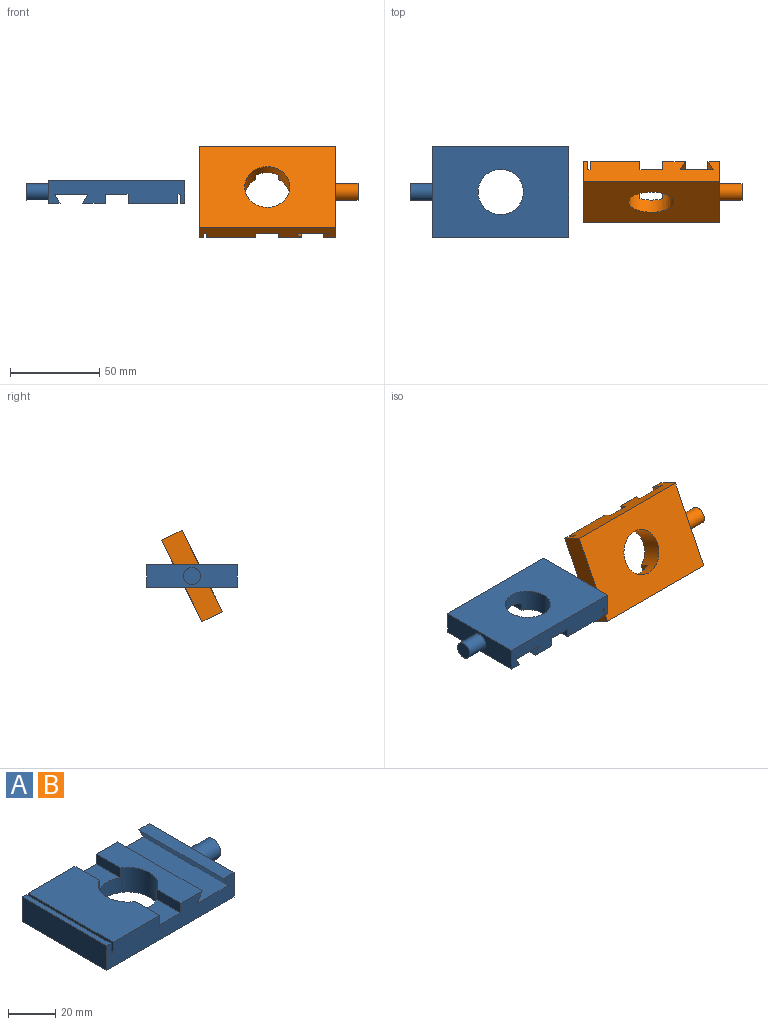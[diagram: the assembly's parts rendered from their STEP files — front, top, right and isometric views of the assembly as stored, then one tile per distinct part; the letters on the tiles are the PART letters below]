
ASSEMBLY  parts=2 mates=1
PART A: 24 faces, bbox 88.9x50.8x12.7 mm
  f0: plane 50.8x6.35mm, normal (0,0,1), area 322.6mm2, adj f1,f2,f7,f21
  f1: plane 76.2x12.7mm, normal (0,-1,0), area 817.4mm2, adj f0,f4,f5,f6,f7,f8,f9,f10
  f2: plane 76.2x12.7mm, normal (0,1,0), area 817.4mm2, adj f0,f4,f5,f6,f7,f8,f9,f13
  f3: cylinder r=12.7mm len=25.4mm, axis (0,0,-1), area 878.3mm2, adj f4,f8,f9,f10,f11,f12,f13,f14
  f4: plane 50.8x27.94mm, normal (0,0,1), area 1320.3mm2, adj f1,f2,f3,f10,f13,f17
  f5: plane 50.8x2.54mm, normal (0,0,1), area 129mm2, adj f1,f2,f6,f16
  f6: plane 50.8x12.7mm, normal (-1,0,0), area 645.2mm2, adj f1,f2,f5,f9
  f7: plane 50.8x12.7mm, normal (1,0,0), area 573.9mm2, adj f0,f1,f2,f9,f22
  f8: plane 50.8x12.7mm, normal (0,0,1), area 546.1mm2, adj f1,f2,f3,f11,f14,f19
  f9: plane 76.2x50.8mm, normal (0,0,-1), area 3364.3mm2, adj f1,f2,f3,f6,f7
  f10: plane 14.4x5.08mm, normal (1,0,0), area 73.2mm2, adj f1,f3,f4,f12
  f11: plane 14.4x5.08mm, normal (-1,0,0), area 73.2mm2, adj f1,f3,f8,f12
  f12: plane 14.4x12.7mm, normal (0,0,1), area 168.3mm2, adj f1,f3,f10,f11
  f13: plane 14.4x5.08mm, normal (1,0,0), area 73.2mm2, adj f2,f3,f4,f15
  f14: plane 14.4x5.08mm, normal (-1,0,0), area 73.2mm2, adj f2,f3,f8,f15
  f15: plane 14.4x12.7mm, normal (0,0,1), area 168.3mm2, adj f2,f3,f13,f14
  f16: plane 50.8x5.08mm, normal (1,0,0), area 258.1mm2, adj f1,f2,f5,f18
  f17: plane 50.8x5.08mm, normal (-1,0,0), area 258.1mm2, adj f1,f2,f4,f18
  f18: plane 50.8x1.27mm, normal (0,0,1), area 64.5mm2, adj f1,f2,f16,f17
  f19: plane 50.8x5.08mm, normal (0.87,0,-0.5), area 298mm2, adj f1,f2,f8,f20
  f20: plane 50.8x18.57mm, normal (0,0,1), area 943.1mm2, adj f1,f2,f19,f21
  f21: plane 50.8x5.08mm, normal (-0.87,0,-0.5), area 298mm2, adj f0,f1,f2,f20
  f22: cylinder r=4.76mm len=12.7mm, axis (-1,0,0), area 380mm2, adj f7,f23
  f23: plane 9.53x9.53mm, normal (1,0,0), area 71.3mm2, adj f22
PART B: same geometry as A
PLACE A rot(axis=(0,1,0),180deg) t=(-137.9,32.41,8.47)mm
PLACE B rot(axis=(-1,0,0),116.3deg) t=(-54.01,28.69,6.17)mm
MATE cylindrical A.f22 <-> B.f22  axis (1,0,0) through (-100.06,33.78,2.12)mm
